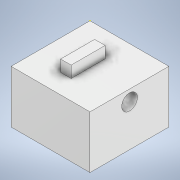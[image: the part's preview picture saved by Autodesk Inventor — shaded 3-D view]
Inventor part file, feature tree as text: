
AUTODESK INVENTOR PART (.ipt)
format: ipt  version: 2022 (Build 260153000, 153)  size: 104,960 bytes
history: native  units: mm
features: sketch x4, extrude x3
ambient origin geometry x8: Origin, YZ Plane, XZ Plane, XY Plane, X Axis, Y Axis, Z Axis, Center Point
bodies: Solid1 (feature_tree)
feature tree (7):
  sketch  "Sketch1"  dims[d2=150.0mm d3=0.0mm d4=30.0mm]
  extrude  "Extrusion1"  Depth=150.0mm
  extrude  "Extrusion2"  Depth=22.0mm TaperAngle=0.0deg
  extrude  "Extrusion3"  [1 undecoded]
  sketch  "Sketch2"  dims[d5=40.75mm d6=0.0mm d8=22.0mm d9=0.0mm]
  sketch  "Sketch3"
  sketch  "Sketch4"
note: 1 required parameter value undecoded (feature->parameter linkage not recoverable at this tier; creation-order binding heuristic only, values carry confidence <= 0.55)
